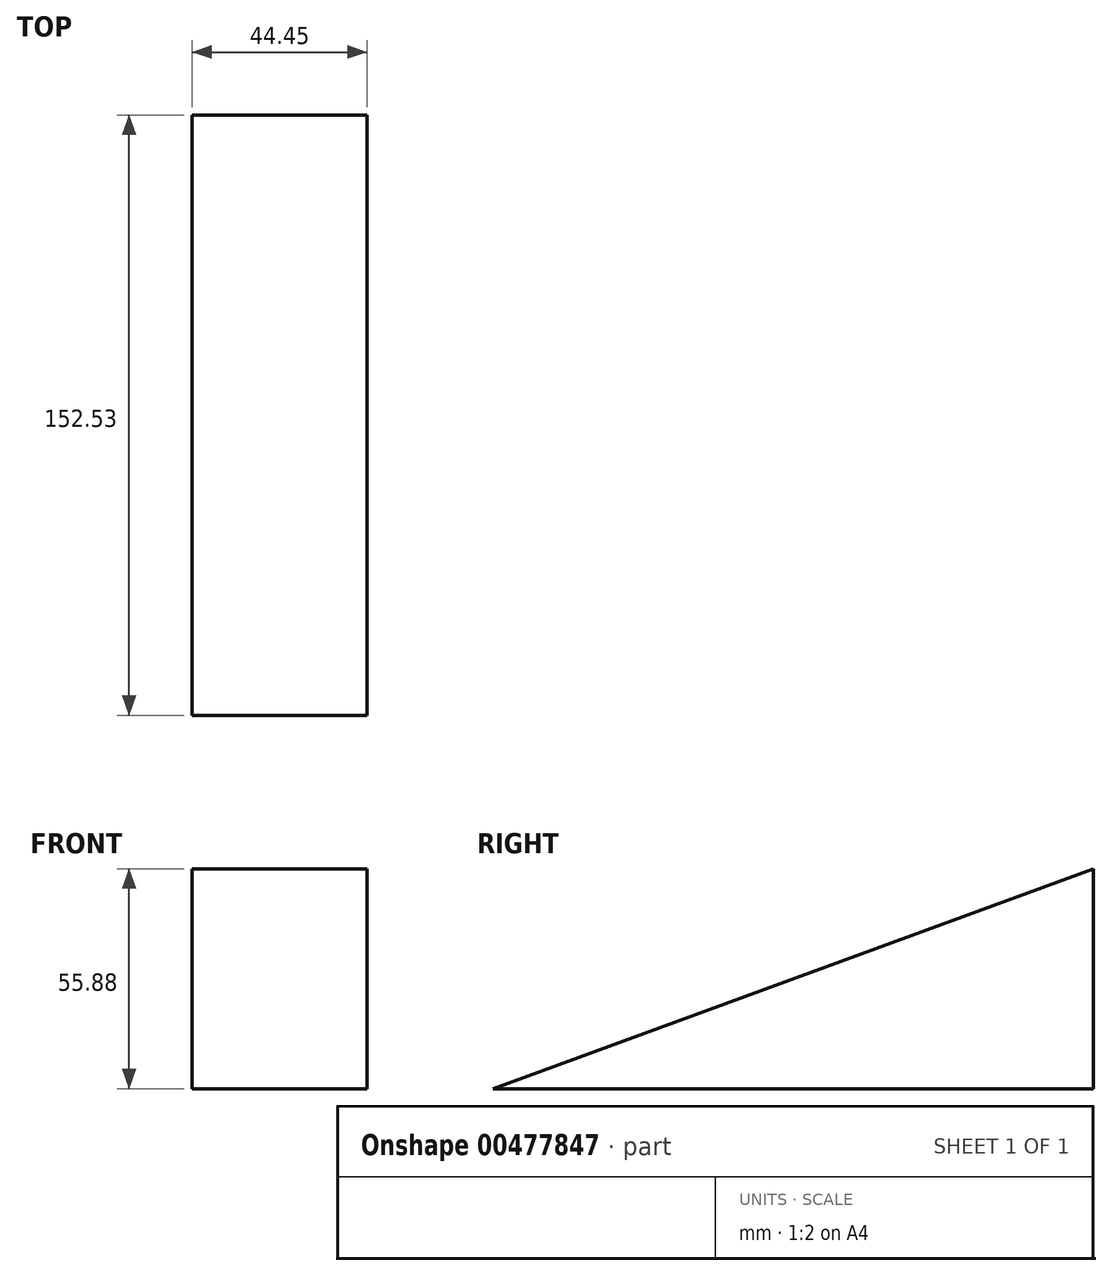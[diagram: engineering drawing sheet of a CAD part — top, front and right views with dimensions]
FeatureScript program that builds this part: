
annotation { "Feature Type Name" : "Feature", "Feature Type Description" : "" }
export const myFeature = defineFeature(function(context is Context, id is Id, definition is map)
    precondition{}
    {
        {
            var Q0;
            Q0=qCreatedBy(makeId("Right.planeOp"),FACE);
            var sketch = newSketch(context, id + "F0", { "sketchPlane" : qUnion([Q0])});
            skLineSegment(sketch, "E0", {"start": v(-76.33, 0) * mm, "end": v(76.2, 55.88) * mm});
            skLineSegment(sketch, "E1", {"start": v(76.2, 55.88) * mm, "end": v(76.2, 0) * mm});
            skLineSegment(sketch, "E2", {"start": v(-76.33, 0) * mm, "end": v(76.2, 0) * mm});
            skSolve(sketch);
        }
        {
            var Q0;
            Q0 = qSketchRegion(id + "F0", true);
            extrude(context, id + "F1", {"entities" : qUnion([Q0]), "depth" : 44.45 * mm});
        }
    });
